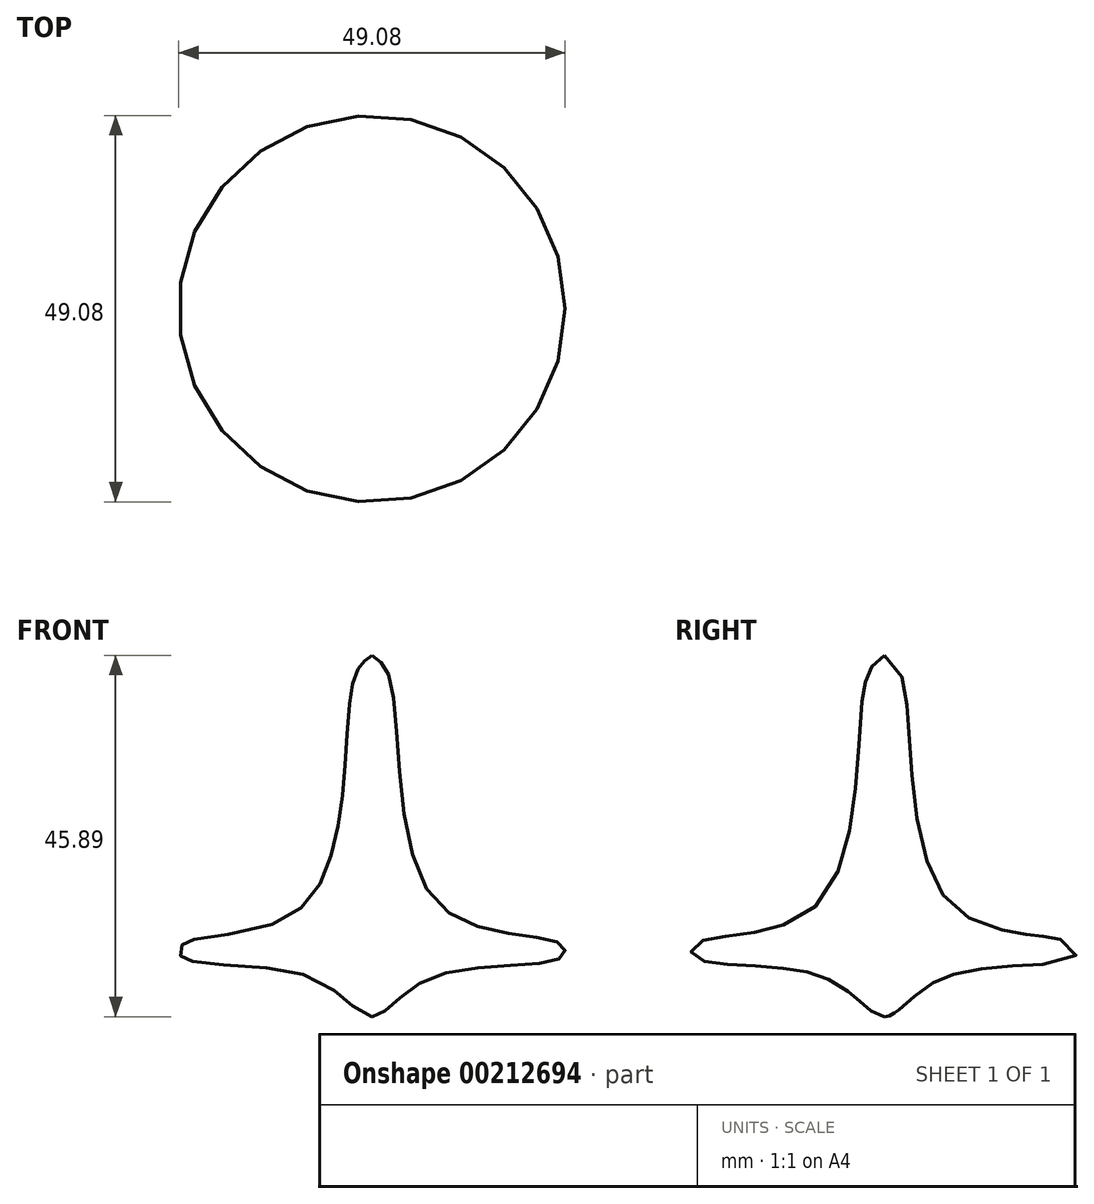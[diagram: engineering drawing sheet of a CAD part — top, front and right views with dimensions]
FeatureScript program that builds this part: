
annotation { "Feature Type Name" : "Feature", "Feature Type Description" : "" }
export const myFeature = defineFeature(function(context is Context, id is Id, definition is map)
    precondition{}
    {
        {
            var Q0;
            Q0=qCreatedBy(makeId("Front.planeOp"),FACE);
            var sketch = newSketch(context, id + "F0", { "sketchPlane" : qUnion([Q0])});
            skFitSpline(sketch, "E0", {"points": [v(0, 0) * mm, v(7.55, 4.96) * mm, v(24.09, 7.52) * mm, v(23.89, 9.3) * mm, v(8.34, 14.4) * mm, v(2.37, 42.72) * mm, v(0, 45.9) * mm], "startDerivative": vector(38.65, 0) * mm, "endDerivative": vector(-25.54, 19.64) * mm});
            skLineSegment(sketch, "E1", {"start": v(0, 45.9) * mm, "end": v(0, 0) * mm});
            skSolve(sketch);
        }
        {
            var Q0;
            Q0=makeQuery(id+"F0.imprint","IMPRINT",FACE,{"disambiguationData":[TD([[makeQuery(id+"F0.imprint","IMPRINT",EDGE,{"derivedFrom":sQuery(id+"F0.wireOp",EDGE,"E0")}),1.0]])]});
            var Q1;
            Q1=sQuery(id+"F0.wireOp",EDGE,"E1");
            revolve(context, id + "F1", {"entities" : qUnion([Q0]), "axis" : qUnion([Q1]), "revolveType" : RevolveType.FULL});
        }
    });
